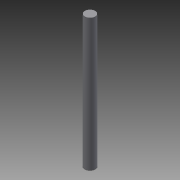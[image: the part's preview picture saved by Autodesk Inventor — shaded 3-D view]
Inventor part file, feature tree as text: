
AUTODESK INVENTOR PART (.ipt)
format: ipt  version: 2014 (Build 180170000, 170)  size: 63,488 bytes
history: native  units: mm
features: extrude x1, sketch x1
ambient origin geometry x8: Origin, YZ Plane, XZ Plane, XY Plane, X Axis, Y Axis, Z Axis, Center Point
bodies: Solid1 (feature_tree)
feature tree (2):
  extrude  "Extrusion1"  Depth=200.0mm TaperAngle=0.0deg
  sketch  "Sketch1"  dims[d0=15.875mm d1=200.0mm d2=0.0mm]
